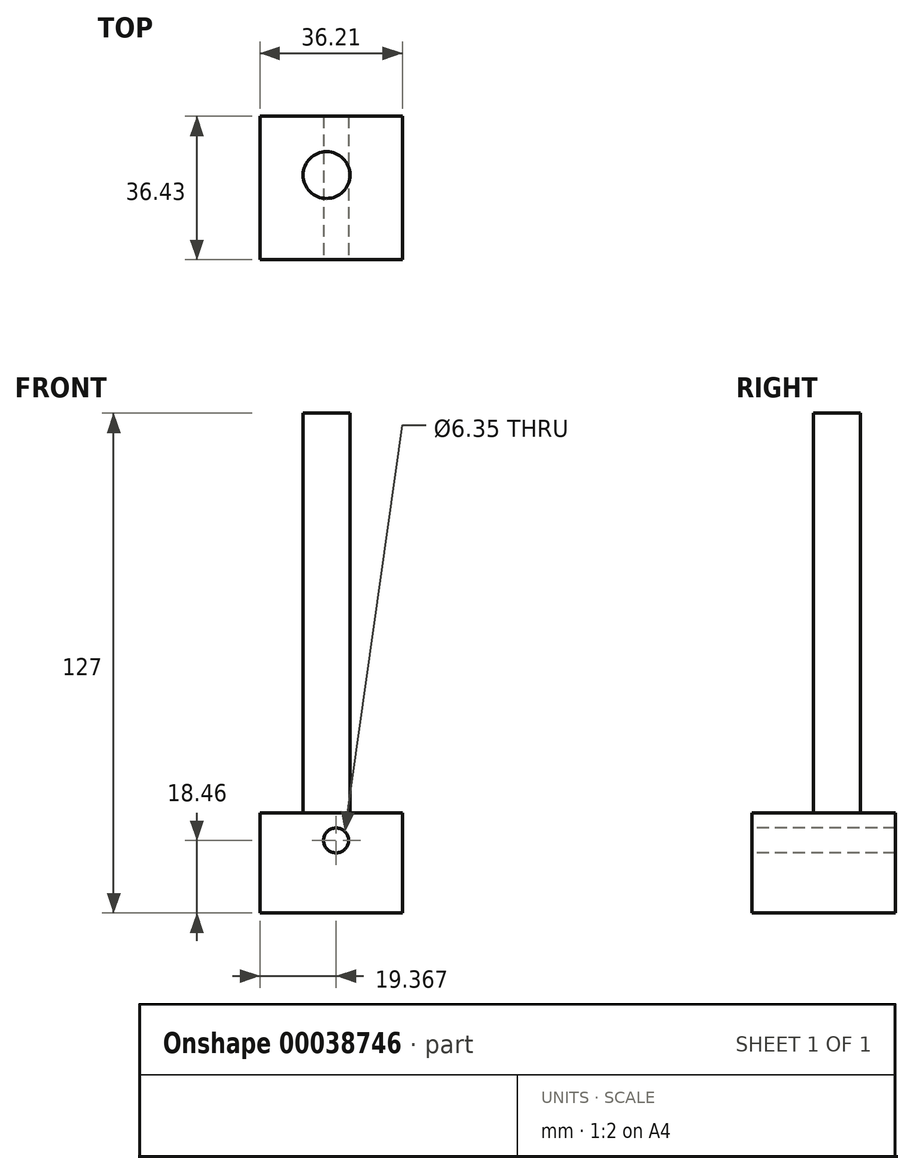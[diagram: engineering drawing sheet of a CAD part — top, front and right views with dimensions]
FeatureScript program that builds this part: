
annotation { "Feature Type Name" : "Feature", "Feature Type Description" : "" }
export const myFeature = defineFeature(function(context is Context, id is Id, definition is map)
    precondition{}
    {
        {
            var Q0;
            Q0=qCreatedBy(makeId("Top.planeOp"),FACE);
            var sketch = newSketch(context, id + "F0", { "sketchPlane" : qUnion([Q0])});
            skLineSegment(sketch, "E0.bottom", {"start": v(0, 1.36) * mm, "end": v(36.2, 1.36) * mm});
            skLineSegment(sketch, "E0.top", {"start": v(0, 37.8) * mm, "end": v(36.2, 37.8) * mm});
            skLineSegment(sketch, "E0.left", {"start": v(0, 1.36) * mm, "end": v(0, 37.8) * mm});
            skLineSegment(sketch, "E0.right", {"start": v(36.2, 1.36) * mm, "end": v(36.2, 37.8) * mm});
            skSolve(sketch);
        }
        {
            var Q0;
            Q0 = qSketchRegion(id + "F0", true);
            extrude(context, id + "F1", {"entities" : qUnion([Q0]), "depth" : 25.4 * mm});
        }
        {
            var Q0;
            Q0=makeQuery(id+"F1.opExtrude","CAP_FACE",FACE,{"disambiguationData":[OSD([sQuery(id+"F0.wireOp",EDGE,"E0.bottom"),sQuery(id+"F0.wireOp",EDGE,"E0.top"),sQuery(id+"F0.wireOp",EDGE,"E0.left"),sQuery(id+"F0.wireOp",EDGE,"E0.right")])],"isStart":false});
            var sketch = newSketch(context, id + "F2", { "sketchPlane" : qUnion([Q0])});
            skCircle(sketch, "E1", {"center": v(16.95, 22.88) * mm, "radius": 5.95 * mm});
            skSolve(sketch);
        }
        {
            var Q0;
            Q0 = qSketchRegion(id + "F2", true);
            extrude(context, id + "F3", {"entities" : qUnion([Q0]), "operationType" : NewBodyOperationType.ADD, "depth" : 101.6 * mm});
        }
        {
            var Q0;
            Q0=makeQuery(id+"F1.opExtrude","SWEPT_FACE",FACE,{"disambiguationData":[OSD([sQuery(id+"F0.wireOp",EDGE,"E0.bottom")])]});
            var sketch = newSketch(context, id + "F4", { "sketchPlane" : qUnion([Q0])});
            skCircle(sketch, "E2", {"center": v(19.37, 18.46) * mm, "radius": 3.18 * mm});
            skSolve(sketch);
        }
        {
            var Q0;
            Q0 = qSketchRegion(id + "F4", true);
            extrude(context, id + "F5", {"entities" : qUnion([Q0]), "operationType" : NewBodyOperationType.REMOVE, "endBound" : BoundingType.THROUGH_ALL, "oppositeDirection" : true, "depth" : 25.4 * mm});
        }
    });
